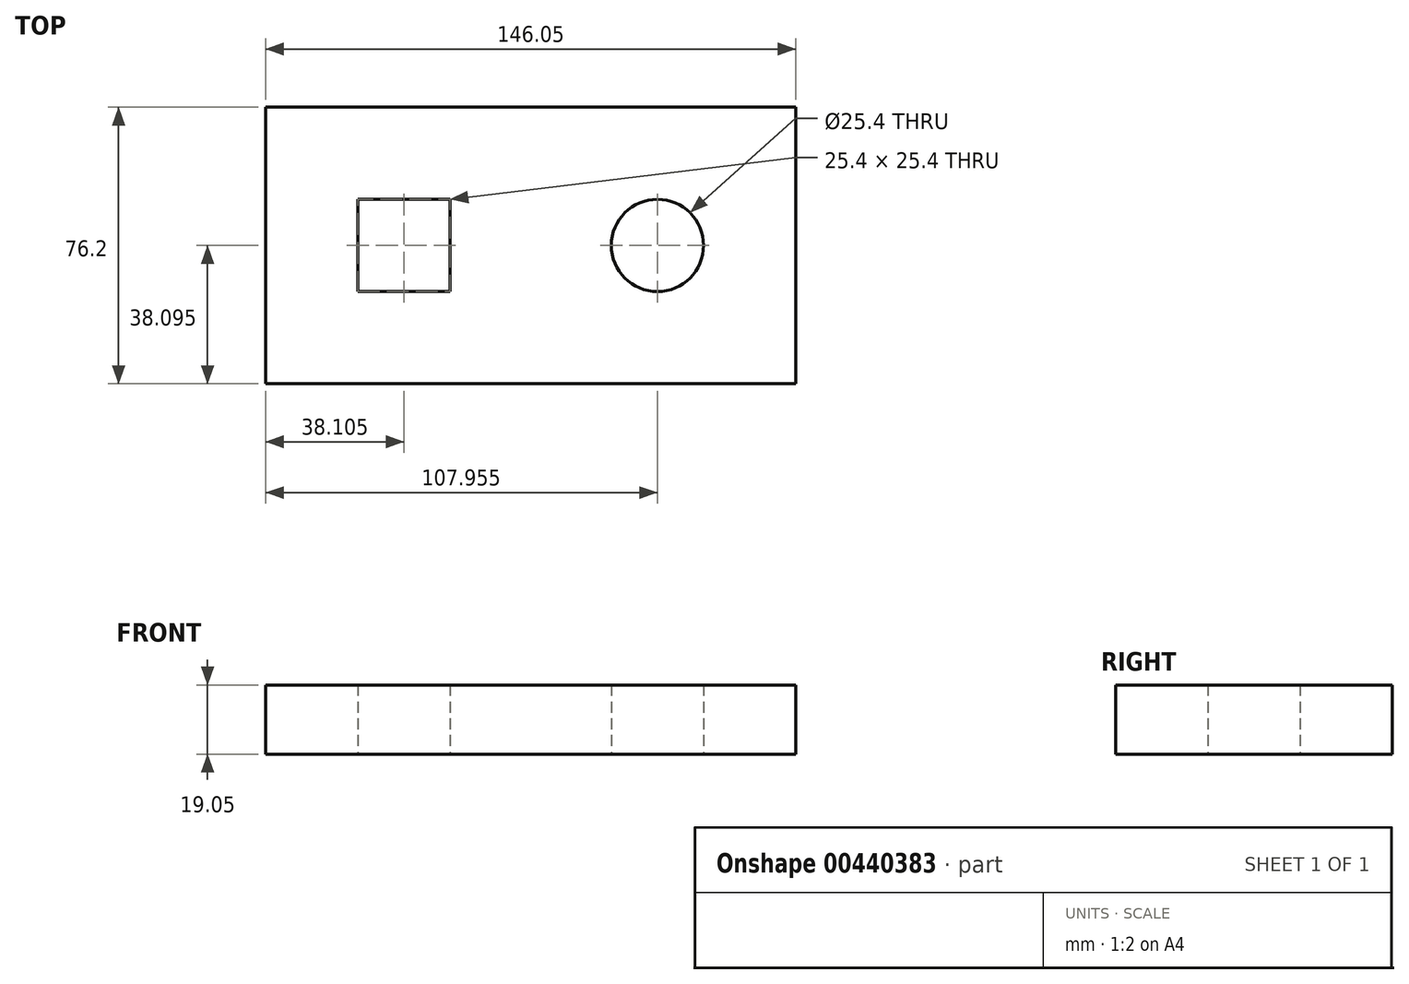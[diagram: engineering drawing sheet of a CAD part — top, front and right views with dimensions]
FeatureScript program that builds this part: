
annotation { "Feature Type Name" : "Feature", "Feature Type Description" : "" }
export const myFeature = defineFeature(function(context is Context, id is Id, definition is map)
    precondition{}
    {
        {
            var Q0;
            Q0=qCreatedBy(makeId("Top.planeOp"),FACE);
            var sketch = newSketch(context, id + "F0", { "sketchPlane" : qUnion([Q0])});
            skLineSegment(sketch, "E0.bottom", {"start": v(-111.1, 59.2) * mm, "end": v(34.94, 59.2) * mm});
            skLineSegment(sketch, "E0.top", {"start": v(-111.1, -17) * mm, "end": v(34.94, -17) * mm});
            skLineSegment(sketch, "E0.left", {"start": v(-111.1, 59.2) * mm, "end": v(-111.1, -17) * mm});
            skLineSegment(sketch, "E0.right", {"start": v(34.94, 59.2) * mm, "end": v(34.94, -17) * mm});
            skLineSegment(sketch, "E1.bottom", {"start": v(-85.7, 8.4) * mm, "end": v(-60.3, 8.4) * mm});
            skLineSegment(sketch, "E1.top", {"start": v(-85.7, 33.8) * mm, "end": v(-60.3, 33.8) * mm});
            skLineSegment(sketch, "E1.left", {"start": v(-85.7, 8.4) * mm, "end": v(-85.7, 33.8) * mm});
            skLineSegment(sketch, "E1.right", {"start": v(-60.3, 8.4) * mm, "end": v(-60.3, 33.8) * mm});
            skCircle(sketch, "E2", {"center": v(-3.16, 21.1) * mm, "radius": 12.7 * mm});
            skSolve(sketch);
        }
        {
            var Q0;
            Q0=makeQuery(id+"F0.imprint","IMPRINT",FACE,{"disambiguationData":[TD([[makeQuery(id+"F0.imprint","IMPRINT",EDGE,{"derivedFrom":sQuery(id+"F0.wireOp",EDGE,"E0.bottom")}),-1.0]])]});
            extrude(context, id + "F1", {"entities" : qUnion([Q0]), "depth" : 19.05 * mm});
        }
    });
